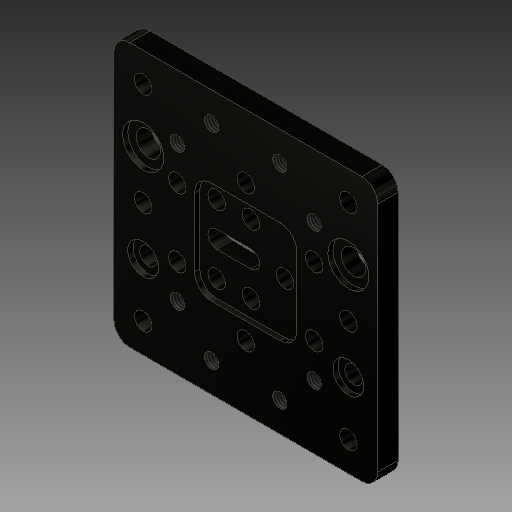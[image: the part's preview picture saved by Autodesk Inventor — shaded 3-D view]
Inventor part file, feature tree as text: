
AUTODESK INVENTOR PART (.ipt)
format: ipt  version: 2019 (Build 230136000, 136)  size: 264,192 bytes
history: native  units: mm
features: thread x8, extrude x2, sketch x2
ambient origin geometry x8: Origin, YZ Plane, XZ Plane, XY Plane, X Axis, Y Axis, Z Axis, Center Point
bodies: Solid1 (feature_tree)
feature tree (12):
  extrude  "Extrusion1"  Depth=77.15mm
  extrude  "Extrusion2"  Depth=5.1mm
  thread  "Thread1"  [1 undecoded]
  thread  "Thread2"  [1 undecoded]
  thread  "Thread3"  [1 undecoded]
  thread  "Thread4"  [1 undecoded]
  thread  "Thread5"  [1 undecoded]
  thread  "Thread6"  [1 undecoded]
  thread  "Thread7"  [1 undecoded]
  thread  "Thread8"  [1 undecoded]
  sketch  "Sketch1"  dims[d0=77.15mm d1=77.15mm]
  sketch  "Sketch2"  dims[d2=4.64mm d3=5.1mm d4=4.2mm d5=8.575mm d6=18.575mm d7=8.575mm d8=7.2mm d9=24.325mm d10=38.575mm d11=52.825mm d12=68.575mm d13=28.575mm d14=18.575mm d15=38.575mm d16=48.545mm d17=58.575mm d18=68.575mm d19=28.575mm d20=10.0mm d21=5.1mm d22=5.1mm d23=6.0mm d24=0.0mm d25=12.0mm d26=9.0mm d27=23.63mm d28=53.53mm d29=23.63mm d30=53.53mm d31=4.92mm d32=1.5mm d33=0.0mm d34=10.0mm d35=0.0mm d36=10.0mm d37=0.0mm d38=10.0mm d39=0.0mm d40=10.0mm d41=0.0mm d42=10.0mm d43=0.0mm d44=10.0mm d45=0.0mm d46=10.0mm d47=0.0mm d48=10.0mm d49=0.0mm]
note: 8 required parameter values undecoded (feature->parameter linkage not recoverable at this tier; creation-order binding heuristic only, values carry confidence <= 0.55)
